# Revit family: Accessory-Grab_Bar-KOHLER-Traditional-K-11872T_1
name_source: partatom
category: Specialty Equipment
revit_build: Autodesk Revit 2017 (Build: 20160225_1515(x64)
units: mm (PartAtom-declared; Revit-internal decimal feet)

## family parameters
Cut with Voids When Loaded = No
Host = Face
OmniClass Number = 23.31.25.00
Part Type = Normal
Room Calculation Point = No
Round Connector Dimension = Use Diameter
Shared = No

## types (2) — shared parameters
ADA Compliant = Yes
Assembly Code = C1030200
Date Modified = 09/03/2020
Default Elevation = 42"
Description = 18 inch Grab Bar
Height = 2 9/16"
Length = 2 7/8"
Manufacturer = KOHLER Co.
Master Format 2014 = 10 28 00
Master Format 2014 Name = Toilet, Bath, and Laundry Accessories
Material = Solid Metal Construction
Product Documentation Link = https://files.kohler.com.cn
Product Name = Traditional
Product Page URL = https://www.kohler.com.cn
URL = http://www.kohler.com.cn
WaterSense Certified = No
Width = 18"

## per-type parameters (varying)
| type | Finish | Model | Type |
| BS-Brushed Stainless | Kohler-Metal-BS-Brushed_Stainless | K-11872T-BS | 1 |
| S-Polished Stainless | Kohler-Metal-S-Polished_Stainless | K-11872T-S | 2 |

## geometry (parser evidence)
native form markers: Sweep x5
no freeform markers — native parametric forms only
